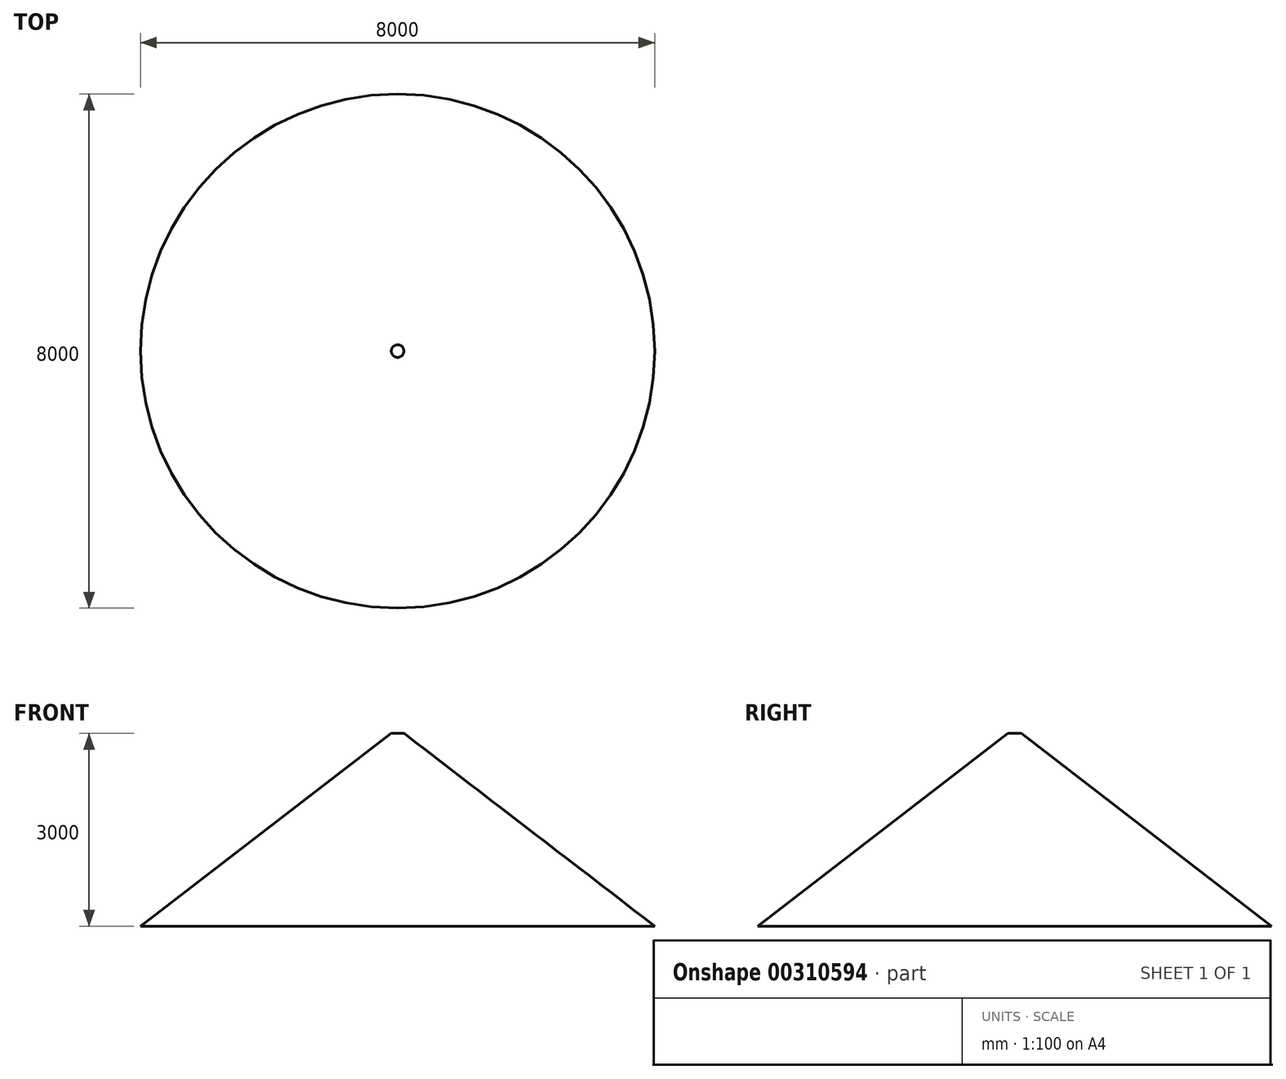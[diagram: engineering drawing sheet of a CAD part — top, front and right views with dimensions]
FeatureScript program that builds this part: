
annotation { "Feature Type Name" : "Feature", "Feature Type Description" : "" }
export const myFeature = defineFeature(function(context is Context, id is Id, definition is map)
    precondition{}
    {
        {
            var Q0;
            Q0=qCreatedBy(makeId("Front.planeOp"),FACE);
            var sketch = newSketch(context, id + "F0", { "sketchPlane" : qUnion([Q0])});
            skLineSegment(sketch, "E0", {"start": v(0, 0) * mm, "end": v(4000, 0) * mm});
            skLineSegment(sketch, "E1", {"start": v(0, 0) * mm, "end": v(0, 3000) * mm, "construction": true});
            skLineSegment(sketch, "E2", {"start": v(0, 3000) * mm, "end": v(100, 3000) * mm});
            skLineSegment(sketch, "E3", {"start": v(100, 3000) * mm, "end": v(4000, 0) * mm});
            skSolve(sketch);
        }
        {
            var Q0;
            Q0=sQuery(id+"F0.wireOp",EDGE,"E2");
            var Q1;
            Q1=sQuery(id+"F0.wireOp",EDGE,"E3");
            var Q2;
            Q2=sQuery(id+"F0.wireOp",EDGE,"E0");
            var Q3;
            Q3=sQuery(id+"F0.wireOp",EDGE,"E1");
            revolve(context, id + "F1", {"bodyType" : ToolBodyType.SURFACE, "surfaceEntities" : qUnion([Q0, Q1, Q2]), "axis" : qUnion([Q3]), "revolveType" : RevolveType.FULL});
        }
        {
            var Q0;
            Q0=makeQuery(id+"F1.opRevolve","SWEPT_EDGE",EDGE,{"disambiguationData":[OSD([sQuery(id+"F0.wireOp",VERTEX,"E3.start")])]});
            chamfer(context, id + "F2", {"entities" : qUnion([Q0]), "width" : 5 * mm, "tangentPropagation" : true});
        }
        {
            var Q0;
            Q0=makeQuery(id+"F2.opChamfer","BLEND_EDGE",EDGE,{"blendedFrom":[makeQuery(id+"F1.opRevolve","SWEPT_EDGE",EDGE,{"disambiguationData":[OSD([sQuery(id+"F0.wireOp",VERTEX,"E3.start")])]}),makeQuery(id+"F1.opRevolve","SWEPT_FACE",FACE,{"disambiguationData":[OSD([sQuery(id+"F0.wireOp",EDGE,"E3")])]})],"blendedInto":[makeQuery(id+"F1.opRevolve","SWEPT_FACE",FACE,{"disambiguationData":[OSD([sQuery(id+"F0.wireOp",EDGE,"E3")])]})]});
            fillet(context, id + "F3", {"entities" : qUnion([Q0]), "radius" : 5 * mm, "tangentPropagation" : true, "allowEdgeOverflow" : false});
        }
    });
